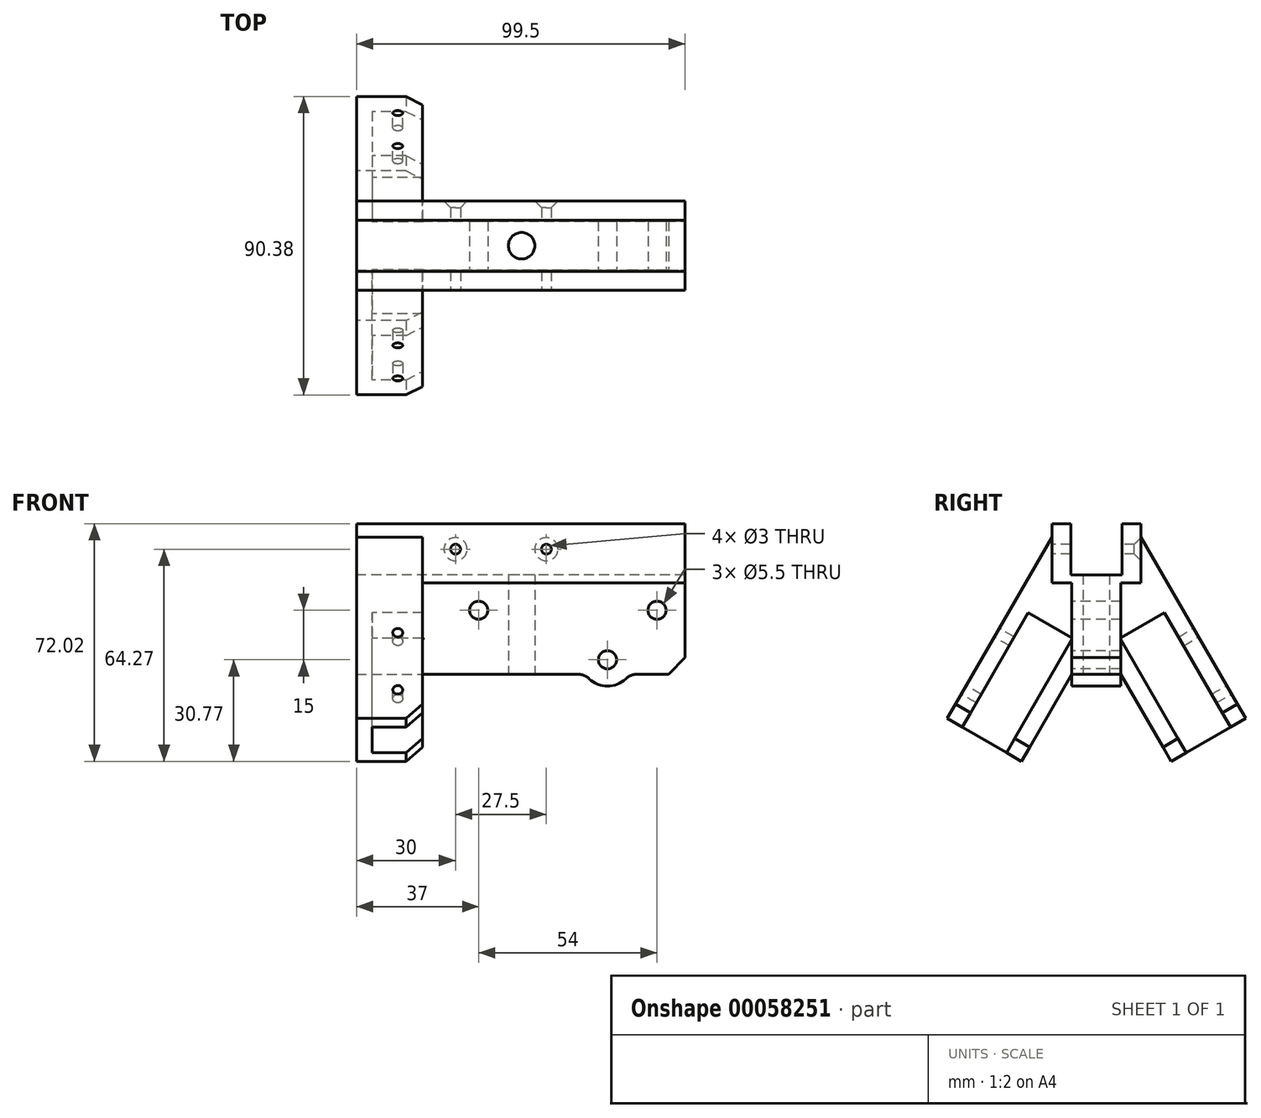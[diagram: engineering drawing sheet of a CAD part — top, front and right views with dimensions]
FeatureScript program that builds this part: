
annotation { "Feature Type Name" : "Feature", "Feature Type Description" : "" }
export const myFeature = defineFeature(function(context is Context, id is Id, definition is map)
    precondition{}
    {
        {
            var Q0;
            Q0=qCreatedBy(makeId("Right.planeOp"),FACE);
            var sketch = newSketch(context, id + "F0", { "sketchPlane" : qUnion([Q0])});
            skLineSegment(sketch, "E0", {"start": v(0, 0) * mm, "end": v(-44.33, -76.78) * mm, "construction": true});
            skLineSegment(sketch, "E1", {"start": v(44.33, -76.78) * mm, "end": v(0, 0) * mm, "construction": true});
            skLineSegment(sketch, "E2.bottom", {"start": v(7.5, -7.5) * mm, "end": v(-7.5, -7.5) * mm});
            skLineSegment(sketch, "E2.top", {"start": v(7.5, 7.5) * mm, "end": v(-7.5, 7.5) * mm});
            skLineSegment(sketch, "E2.left", {"start": v(7.5, -7.5) * mm, "end": v(7.5, 7.5) * mm});
            skLineSegment(sketch, "E2.right", {"start": v(-7.5, -7.5) * mm, "end": v(-7.5, 7.5) * mm});
            skPoint(sketch, "E2.middle", {"position": v(0, 0) * mm});
            skPoint(sketch, "E3", {"position": v(13.5, -23.37) * mm});
            skLineSegment(sketch, "E4", {"start": v(0, 0) * mm, "end": v(0, -80.5) * mm, "construction": true});
            skLineSegment(sketch, "E5", {"start": v(7, -27.12) * mm, "end": v(20, -19.62) * mm, "construction": true});
            skLineSegment(sketch, "E6", {"start": v(8.37, 12.5) * mm, "end": v(45.19, -51.27) * mm});
            skLineSegment(sketch, "E7", {"start": v(45.19, -51.27) * mm, "end": v(33.5, -58.02) * mm, "construction": true});
            skLineSegment(sketch, "E8.MirrorCS", {"start": v(-8.37, 12.5) * mm, "end": v(-45.19, -51.27) * mm});
            skLineSegment(sketch, "E9", {"start": v(-8.37, 12.5) * mm, "end": v(8.37, 12.5) * mm});
            skLineSegment(sketch, "E10", {"start": v(0, -25) * mm, "end": v(22.67, -64.27) * mm});
            skLineSegment(sketch, "E11.MirrorCS", {"start": v(0, -25) * mm, "end": v(-22.67, -64.27) * mm});
            skLineSegment(sketch, "E12", {"start": v(-45.19, -51.27) * mm, "end": v(-22.67, -64.27) * mm});
            skLineSegment(sketch, "E13", {"start": v(22.67, -64.27) * mm, "end": v(45.19, -51.27) * mm});
            skSolve(sketch);
        }
        {
            var Q0;
            Q0 = qSketchRegion(id + "F0", true);
            extrude(context, id + "F1", {"entities" : qUnion([Q0]), "depth" : 20 * mm});
        }
        {
            var Q0;
            Q0=makeQuery(id+"F1.opExtrude","CAP_FACE",FACE,{"disambiguationData":[OSD([sQuery(id+"F0.wireOp",EDGE,"E2.bottom"),sQuery(id+"F0.wireOp",EDGE,"E2.top"),sQuery(id+"F0.wireOp",EDGE,"E2.left"),sQuery(id+"F0.wireOp",EDGE,"E2.right"),sQuery(id+"F0.wireOp",EDGE,"E6"),sQuery(id+"F0.wireOp",EDGE,"E8.MirrorCS"),sQuery(id+"F0.wireOp",EDGE,"E9"),sQuery(id+"F0.wireOp",EDGE,"E10"),sQuery(id+"F0.wireOp",EDGE,"E11.MirrorCS"),sQuery(id+"F0.wireOp",EDGE,"E12"),sQuery(id+"F0.wireOp",EDGE,"E13")])],"isStart":false});
            var sketch = newSketch(context, id + "F2", { "sketchPlane" : qUnion([Q0])});
            skLineSegment(sketch, "E14", {"start": v(0, 0) * mm, "end": v(0, -66.35) * mm, "construction": true});
            skLineSegment(sketch, "E15", {"start": v(-40.42, -54.02) * mm, "end": v(-27.43, -61.52) * mm});
            skLineSegment(sketch, "E16", {"start": v(-27.43, -61.52) * mm, "end": v(-7.43, -26.87) * mm});
            skLineSegment(sketch, "E17", {"start": v(-7.43, -26.87) * mm, "end": v(-20.42, -19.37) * mm});
            skLineSegment(sketch, "E18", {"start": v(-20.42, -19.37) * mm, "end": v(-40.42, -54.02) * mm});
            skPoint(sketch, "E19", {"position": v(-33.93, -57.77) * mm});
            skLineSegment(sketch, "E20.MirrorCS", {"start": v(40.42, -54.02) * mm, "end": v(27.43, -61.52) * mm});
            skLineSegment(sketch, "E21.MirrorCS", {"start": v(27.43, -61.52) * mm, "end": v(7.43, -26.87) * mm});
            skLineSegment(sketch, "E22.MirrorCS", {"start": v(20.42, -19.37) * mm, "end": v(40.42, -54.02) * mm});
            skLineSegment(sketch, "E23.MirrorCS", {"start": v(7.43, -26.87) * mm, "end": v(20.42, -19.37) * mm});
            skSolve(sketch);
        }
        {
            var Q0;
            Q0 = qSketchRegion(id + "F2", true);
            extrude(context, id + "F3", {"entities" : qUnion([Q0]), "operationType" : NewBodyOperationType.REMOVE, "oppositeDirection" : true, "depth" : 15 * mm});
        }
        {
            var Q0;
            Q0=makeQuery(id+"F1.opExtrude","SWEPT_FACE",FACE,{"disambiguationData":[OSD([sQuery(id+"F0.wireOp",EDGE,"E8.MirrorCS")])]});
            var sketch = newSketch(context, id + "F4", { "sketchPlane" : qUnion([Q0])});
            skLineSegment(sketch, "E24.0", {"start": v(5, -67) * mm, "end": v(20, -67) * mm, "construction": true});
            skLineSegment(sketch, "E24.1", {"start": v(5, -27) * mm, "end": v(20, -27) * mm, "construction": true});
            skLineSegment(sketch, "E25", {"start": v(12.5, -27) * mm, "end": v(12.5, -67) * mm, "construction": true});
            skCircle(sketch, "E26", {"center": v(12.5, -37) * mm, "radius": 1.5 * mm});
            skCircle(sketch, "E27", {"center": v(12.5, -57) * mm, "radius": 1.5 * mm});
            skSolve(sketch);
        }
        {
            var Q0;
            Q0 = qSketchRegion(id + "F4", true);
            extrude(context, id + "F5", {"entities" : qUnion([Q0]), "operationType" : NewBodyOperationType.REMOVE, "endBound" : BoundingType.UP_TO_NEXT, "oppositeDirection" : true, "depth" : 25 * mm});
        }
        {
            var Q0;
            Q0=makeQuery(id+"F1.opExtrude","SWEPT_FACE",FACE,{"disambiguationData":[OSD([sQuery(id+"F0.wireOp",EDGE,"E6")])]});
            var sketch = newSketch(context, id + "F6", { "sketchPlane" : qUnion([Q0])});
            skLineSegment(sketch, "E28.0", {"start": v(-5, -67) * mm, "end": v(-20, -67) * mm, "construction": true});
            skLineSegment(sketch, "E28.1", {"start": v(-5, -27) * mm, "end": v(-20, -27) * mm, "construction": true});
            skLineSegment(sketch, "E29", {"start": v(-12.5, -67) * mm, "end": v(-12.5, -27) * mm, "construction": true});
            skCircle(sketch, "E30", {"center": v(-12.5, -57) * mm, "radius": 1.5 * mm});
            skCircle(sketch, "E31", {"center": v(-12.5, -37) * mm, "radius": 1.5 * mm});
            skSolve(sketch);
        }
        {
            var Q0;
            Q0 = qSketchRegion(id + "F6", true);
            extrude(context, id + "F7", {"entities" : qUnion([Q0]), "operationType" : NewBodyOperationType.REMOVE, "endBound" : BoundingType.UP_TO_NEXT, "oppositeDirection" : true, "depth" : 25 * mm});
        }
        {
            var Q0;
            Q0=makeQuery(id+"F1.opExtrude","CAP_FACE",FACE,{"disambiguationData":[OSD([sQuery(id+"F0.wireOp",EDGE,"E2.bottom"),sQuery(id+"F0.wireOp",EDGE,"E2.top"),sQuery(id+"F0.wireOp",EDGE,"E2.left"),sQuery(id+"F0.wireOp",EDGE,"E2.right"),sQuery(id+"F0.wireOp",EDGE,"E6"),sQuery(id+"F0.wireOp",EDGE,"E8.MirrorCS"),sQuery(id+"F0.wireOp",EDGE,"E9"),sQuery(id+"F0.wireOp",EDGE,"E10"),sQuery(id+"F0.wireOp",EDGE,"E11.MirrorCS"),sQuery(id+"F0.wireOp",EDGE,"E12"),sQuery(id+"F0.wireOp",EDGE,"E13")])],"isStart":false});
            var sketch = newSketch(context, id + "F8", { "sketchPlane" : qUnion([Q0])});
            skLineSegment(sketch, "E32.0", {"start": v(-8.37, 12.5) * mm, "end": v(8.37, 12.5) * mm});
            skLineSegment(sketch, "E32.1", {"start": v(-7.5, -7.5) * mm, "end": v(-7.5, 7.5) * mm});
            skLineSegment(sketch, "E32.2", {"start": v(7.5, 7.5) * mm, "end": v(-7.5, 7.5) * mm});
            skLineSegment(sketch, "E32.3", {"start": v(7.5, -7.5) * mm, "end": v(7.5, 7.5) * mm});
            skLineSegment(sketch, "E32.4", {"start": v(7.5, -7.5) * mm, "end": v(-7.5, -7.5) * mm});
            skLineSegment(sketch, "E33", {"start": v(-8.37, 12.5) * mm, "end": v(-13.5, 3.62) * mm});
            skLineSegment(sketch, "E34", {"start": v(-13.5, 3.62) * mm, "end": v(-13.5, -23.37) * mm});
            skLineSegment(sketch, "E35", {"start": v(0, 7.5) * mm, "end": v(0, 0) * mm, "construction": true});
            skLineSegment(sketch, "E36", {"start": v(-13.5, -23.37) * mm, "end": v(-7.43, -26.87) * mm});
            skLineSegment(sketch, "E37.MirrorCS", {"start": v(8.37, 12.5) * mm, "end": v(13.5, 3.62) * mm});
            skLineSegment(sketch, "E38.MirrorCS", {"start": v(13.5, 3.62) * mm, "end": v(13.5, -23.37) * mm});
            skLineSegment(sketch, "E39.MirrorCS", {"start": v(13.5, -23.37) * mm, "end": v(7.43, -26.87) * mm});
            skLineSegment(sketch, "E40", {"start": v(-7.43, -26.87) * mm, "end": v(7.43, -26.87) * mm});
            skSolve(sketch);
        }
        {
            var Q0;
            Q0 = qSketchRegion(id + "F8", true);
            extrude(context, id + "F9", {"entities" : qUnion([Q0]), "operationType" : NewBodyOperationType.ADD, "depth" : 47.5 * mm});
        }
        {
            var Q0;
            Q0=makeQuery(id+"F9.opExtrude","SWEPT_FACE",FACE,{"disambiguationData":[OSD([sQuery(id+"F8.wireOp",EDGE,"E40")])]});
            var sketch = newSketch(context, id + "F10", { "sketchPlane" : qUnion([Q0])});
            skLineSegment(sketch, "E41", {"start": v(50, 7.43) * mm, "end": v(50, -7.43) * mm, "construction": true});
            skCircle(sketch, "E42", {"center": v(50, 0) * mm, "radius": 4 * mm});
            skSolve(sketch);
        }
        {
            var Q0;
            Q0 = qSketchRegion(id + "F10", true);
            extrude(context, id + "F11", {"entities" : qUnion([Q0]), "operationType" : NewBodyOperationType.REMOVE, "endBound" : BoundingType.UP_TO_NEXT, "oppositeDirection" : true, "depth" : 25 * mm});
        }
        {
            var Q0;
            Q0=makeQuery(id+"F9.opExtrude","CAP_FACE",FACE,{"disambiguationData":[OSD([sQuery(id+"F8.wireOp",EDGE,"E32.0"),sQuery(id+"F8.wireOp",EDGE,"E32.1"),sQuery(id+"F8.wireOp",EDGE,"E32.2"),sQuery(id+"F8.wireOp",EDGE,"E32.3"),sQuery(id+"F8.wireOp",EDGE,"E32.4"),sQuery(id+"F8.wireOp",EDGE,"E33"),sQuery(id+"F8.wireOp",EDGE,"E34"),sQuery(id+"F8.wireOp",EDGE,"E36"),sQuery(id+"F8.wireOp",EDGE,"E37.MirrorCS"),sQuery(id+"F8.wireOp",EDGE,"E38.MirrorCS"),sQuery(id+"F8.wireOp",EDGE,"E39.MirrorCS"),sQuery(id+"F8.wireOp",EDGE,"E40")])],"isStart":false});
            var sketch = newSketch(context, id + "F12", { "sketchPlane" : qUnion([Q0])});
            skLineSegment(sketch, "E43.0", {"start": v(-4, -7.5) * mm, "end": v(4, -7.5) * mm, "construction": true});
            skLineSegment(sketch, "E44", {"start": v(-4, -7.5) * mm, "end": v(-12.87, -7.5) * mm, "construction": true});
            skPoint(sketch, "E45", {"position": v(-7.87, -7.5) * mm});
            skLineSegment(sketch, "E46", {"start": v(-7.87, -7.5) * mm, "end": v(-7.87, -25.06) * mm, "construction": true});
            skLineSegment(sketch, "E47", {"start": v(-24.1, -18.5) * mm, "end": v(2.06, -18.5) * mm, "construction": true});
            skLineSegment(sketch, "E48.0", {"start": v(-7.43, -26.87) * mm, "end": v(-13.5, -23.37) * mm});
            skLineSegment(sketch, "E49", {"start": v(-13.5, -23.37) * mm, "end": v(-13.5, -10.25) * mm});
            skLineSegment(sketch, "E50", {"start": v(-13.5, -10.25) * mm, "end": v(-7.43, -10.25) * mm});
            skLineSegment(sketch, "E51", {"start": v(-7.43, -10.25) * mm, "end": v(-7.43, -26.87) * mm});
            skLineSegment(sketch, "E52", {"start": v(0, 0) * mm, "end": v(0, 7.5) * mm, "construction": true});
            skLineSegment(sketch, "E53.MirrorCS", {"start": v(7.43, -26.87) * mm, "end": v(13.5, -23.37) * mm});
            skLineSegment(sketch, "E54.MirrorCS", {"start": v(7.43, -10.25) * mm, "end": v(7.43, -26.87) * mm});
            skLineSegment(sketch, "E55.MirrorCS", {"start": v(13.5, -10.25) * mm, "end": v(7.43, -10.25) * mm});
            skLineSegment(sketch, "E56.MirrorCS", {"start": v(13.5, -23.37) * mm, "end": v(13.5, -10.25) * mm});
            skSolve(sketch);
        }
        {
            var Q0;
            Q0 = qSketchRegion(id + "F12", true);
            var Q1;
            {var subQ0=sQuery(id+"F0.wireOp",EDGE,"E8.MirrorCS");var subQ1=sQuery(id+"F0.wireOp",EDGE,"E12");Q1=makeQuery(id+"F9.boolean.opBoolean","SPLIT",FACE,{"disambiguationData":[TD([makeQuery(id+"F1.opExtrude","SWEPT_FACE",FACE,{"disambiguationData":[OSD([subQ0])]})])],"derivedFrom":makeQuery(id+"F1.opExtrude","CAP_FACE",FACE,{"disambiguationData":[OSD([sQuery(id+"F0.wireOp",EDGE,"E2.bottom"),sQuery(id+"F0.wireOp",EDGE,"E2.top"),sQuery(id+"F0.wireOp",EDGE,"E2.left"),sQuery(id+"F0.wireOp",EDGE,"E2.right"),sQuery(id+"F0.wireOp",EDGE,"E6"),subQ0,sQuery(id+"F0.wireOp",EDGE,"E9"),sQuery(id+"F0.wireOp",EDGE,"E10"),sQuery(id+"F0.wireOp",EDGE,"E11.MirrorCS"),subQ1,sQuery(id+"F0.wireOp",EDGE,"E13")])],"isStart":false})});}
            extrude(context, id + "F13", {"entities" : qUnion([Q0]), "operationType" : NewBodyOperationType.REMOVE, "endBound" : BoundingType.UP_TO_SURFACE, "oppositeDirection" : true, "endBoundEntityFace" : qUnion([Q1]), "depth" : 25 * mm});
        }
        {
            var Q0;
            Q0=makeQuery(id+"F13.boolean.opBoolean","COPY",FACE,{"derivedFrom":makeQuery(id+"F13.opExtrude","SWEPT_FACE",FACE,{"disambiguationData":[OSD([sQuery(id+"F12.wireOp",EDGE,"E51")])]})});
            var sketch = newSketch(context, id + "F14", { "sketchPlane" : qUnion([Q0])});
            skLineSegment(sketch, "E57.0", {"start": v(54, -26.87) * mm, "end": v(46, -26.87) * mm, "construction": true});
            skCircle(sketch, "E58", {"center": v(37, -18.5) * mm, "radius": 2.75 * mm});
            skLineSegment(sketch, "E59", {"start": v(50, -26.87) * mm, "end": v(50, -10.25) * mm, "construction": true});
            skLineSegment(sketch, "E60", {"start": v(33, -26.87) * mm, "end": v(33, -10.25) * mm, "construction": true});
            skCircle(sketch, "E61", {"center": v(37, -18.5) * mm, "radius": 8 * mm, "construction": true});
            skCircle(sketch, "E62", {"center": v(37, -18.5) * mm, "radius": 7.5 * mm, "construction": true});
            skPoint(sketch, "E63", {"position": v(29.5, -18.5) * mm});
            skSolve(sketch);
        }
        {
            var Q0;
            Q0 = qSketchRegion(id + "F14", true);
            extrude(context, id + "F15", {"entities" : qUnion([Q0]), "operationType" : NewBodyOperationType.REMOVE, "endBound" : BoundingType.THROUGH_ALL, "oppositeDirection" : true, "depth" : 25 * mm});
        }
        {
            var Q0;
            Q0=makeQuery(id+"F9.opExtrude","CAP_FACE",FACE,{"disambiguationData":[OSD([sQuery(id+"F8.wireOp",EDGE,"E32.0"),sQuery(id+"F8.wireOp",EDGE,"E32.1"),sQuery(id+"F8.wireOp",EDGE,"E32.2"),sQuery(id+"F8.wireOp",EDGE,"E32.3"),sQuery(id+"F8.wireOp",EDGE,"E32.4"),sQuery(id+"F8.wireOp",EDGE,"E33"),sQuery(id+"F8.wireOp",EDGE,"E34"),sQuery(id+"F8.wireOp",EDGE,"E36"),sQuery(id+"F8.wireOp",EDGE,"E37.MirrorCS"),sQuery(id+"F8.wireOp",EDGE,"E38.MirrorCS"),sQuery(id+"F8.wireOp",EDGE,"E39.MirrorCS"),sQuery(id+"F8.wireOp",EDGE,"E40")])],"isStart":true});
            var Q1;
            Q1=makeQuery(id+"F1.opExtrude","CAP_FACE",FACE,{"disambiguationData":[OSD([sQuery(id+"F0.wireOp",EDGE,"E2.bottom"),sQuery(id+"F0.wireOp",EDGE,"E2.top"),sQuery(id+"F0.wireOp",EDGE,"E2.left"),sQuery(id+"F0.wireOp",EDGE,"E2.right"),sQuery(id+"F0.wireOp",EDGE,"E6"),sQuery(id+"F0.wireOp",EDGE,"E8.MirrorCS"),sQuery(id+"F0.wireOp",EDGE,"E9"),sQuery(id+"F0.wireOp",EDGE,"E10"),sQuery(id+"F0.wireOp",EDGE,"E11.MirrorCS"),sQuery(id+"F0.wireOp",EDGE,"E12"),sQuery(id+"F0.wireOp",EDGE,"E13")])],"isStart":true});
            extrude(context, id + "F16", {"entities" : qUnion([Q0]), "operationType" : NewBodyOperationType.ADD, "endBound" : BoundingType.UP_TO_SURFACE, "endBoundEntityFace" : qUnion([Q1]), "depth" : 25 * mm});
        }
        {
            var Q0;
            {var subQ0=sQuery(id+"F8.wireOp",EDGE,"E40");Q0=makeQuery(id+"F16.boolean.opBoolean","MERGE",FACE,{"derivedFrom":[makeQuery(id+"F9.opExtrude","SWEPT_FACE",FACE,{"disambiguationData":[OSD([subQ0])]}),makeQuery(id+"F16.opExtrude","SWEPT_FACE",FACE,{"disambiguationData":[OSD([subQ0])]})]});}
            var sketch = newSketch(context, id + "F17", { "sketchPlane" : qUnion([Q0])});
            skLineSegment(sketch, "E64.bottom", {"start": v(67.5, 7.43) * mm, "end": v(0, 7.43) * mm});
            skLineSegment(sketch, "E64.top", {"start": v(67.5, -7.43) * mm, "end": v(0, -7.43) * mm});
            skLineSegment(sketch, "E64.left", {"start": v(67.5, 7.43) * mm, "end": v(67.5, -7.43) * mm});
            skLineSegment(sketch, "E64.right", {"start": v(0, 7.43) * mm, "end": v(0, -7.43) * mm});
            skCircle(sketch, "E65.0", {"center": v(50, 0) * mm, "radius": 4 * mm});
            skSolve(sketch);
        }
        {
            var Q0;
            Q0 = qSketchRegion(id + "F17", true);
            var Q1;
            Q1=makeQuery(id+"F1.opExtrude","SWEPT_FACE",FACE,{"disambiguationData":[OSD([sQuery(id+"F0.wireOp",EDGE,"E11.MirrorCS")])]});
            var Q2;
            Q2=makeQuery(id+"F1.opExtrude","CAP_VERTEX",VERTEX,{"disambiguationData":[OSD([sQuery(id+"F0.wireOp",EDGE,"E11.MirrorCS"),sQuery(id+"F0.wireOp",EDGE,"E12")])],"isStart":false});
            extrude(context, id + "F18", {"entities" : qUnion([Q0]), "operationType" : NewBodyOperationType.ADD, "endBound" : BoundingType.UP_TO_VERTEX, "endBoundEntityFace" : qUnion([Q1]), "endBoundEntityVertex" : qUnion([Q2]), "depth" : 25 * mm});
        }
        {
            var Q0;
            {var subQ0=sQuery(id+"F0.wireOp",EDGE,"E13");var subQ1=sQuery(id+"F0.wireOp",EDGE,"E12");var subQ2=sQuery(id+"F0.wireOp",EDGE,"E11.MirrorCS");var subQ3=sQuery(id+"F0.wireOp",EDGE,"E10");var subQ4=sQuery(id+"F0.wireOp",EDGE,"E9");var subQ5=sQuery(id+"F0.wireOp",EDGE,"E8.MirrorCS");var subQ6=sQuery(id+"F0.wireOp",EDGE,"E6");var subQ7=sQuery(id+"F0.wireOp",EDGE,"E2.right");var subQ8=sQuery(id+"F0.wireOp",EDGE,"E2.left");var subQ9=sQuery(id+"F0.wireOp",EDGE,"E2.top");var subQ10=sQuery(id+"F0.wireOp",EDGE,"E2.bottom");Q0=makeQuery(id+"F18.boolean.opBoolean","MERGE",FACE,{"derivedFrom":[makeQuery(id+"F16.boolean.opBoolean","MERGE",FACE,{"derivedFrom":[makeQuery(id+"F1.opExtrude","CAP_FACE",FACE,{"disambiguationData":[OSD([subQ10,subQ9,subQ8,subQ7,subQ6,subQ5,subQ4,subQ3,subQ2,subQ1,subQ0])],"isStart":true}),makeQuery(id+"F16.opExtrude","CAP_FACE",FACE,{"disambiguationData":[OSD([subQ10,subQ9,subQ8,subQ7,subQ6,subQ5,subQ4,subQ3,subQ2,subQ1,subQ0])],"isStart":false})]}),makeQuery(id+"F18.opExtrude","SWEPT_FACE",FACE,{"disambiguationData":[OSD([sQuery(id+"F17.wireOp",EDGE,"E64.right")])]})]});}
            var sketch = newSketch(context, id + "F19", { "sketchPlane" : qUnion([Q0])});
            skLineSegment(sketch, "E66.bottom", {"start": v(7.43, -64.27) * mm, "end": v(-7.43, -64.27) * mm});
            skLineSegment(sketch, "E66.top", {"start": v(7.43, -37.87) * mm, "end": v(-7.43, -37.87) * mm});
            skLineSegment(sketch, "E66.left", {"start": v(7.43, -64.27) * mm, "end": v(7.43, -37.87) * mm});
            skLineSegment(sketch, "E66.right", {"start": v(-7.43, -64.27) * mm, "end": v(-7.43, -37.87) * mm});
            skSolve(sketch);
        }
        {
            var Q0;
            Q0 = qSketchRegion(id + "F19", true);
            extrude(context, id + "F20", {"entities" : qUnion([Q0]), "operationType" : NewBodyOperationType.REMOVE, "endBound" : BoundingType.THROUGH_ALL, "oppositeDirection" : true, "depth" : 25 * mm});
        }
        {
            var Q0;
            {var subQ0=sQuery(id+"F0.wireOp",EDGE,"E12");var subQ1=sQuery(id+"F0.wireOp",EDGE,"E8.MirrorCS");Q0=makeQuery(id+"F3.boolean.opBoolean","SPLIT",EDGE,{"disambiguationData":[TD([makeQuery(id+"F1.opExtrude","SWEPT_FACE",FACE,{"disambiguationData":[OSD([subQ1])]})])],"derivedFrom":makeQuery(id+"F1.opExtrude","CAP_EDGE",EDGE,{"disambiguationData":[OSD([subQ0])],"isStart":false})});}
            var Q1;
            {var subQ0=sQuery(id+"F0.wireOp",EDGE,"E12");var subQ1=sQuery(id+"F0.wireOp",EDGE,"E11.MirrorCS");Q1=makeQuery(id+"F3.boolean.opBoolean","SPLIT",EDGE,{"disambiguationData":[TD([makeQuery(id+"F1.opExtrude","SWEPT_FACE",FACE,{"disambiguationData":[OSD([subQ1])]})])],"derivedFrom":makeQuery(id+"F1.opExtrude","CAP_EDGE",EDGE,{"disambiguationData":[OSD([subQ0])],"isStart":false})});}
            var Q2;
            {var subQ0=sQuery(id+"F0.wireOp",EDGE,"E13");var subQ1=sQuery(id+"F0.wireOp",EDGE,"E10");Q2=makeQuery(id+"F3.boolean.opBoolean","SPLIT",EDGE,{"disambiguationData":[TD([makeQuery(id+"F1.opExtrude","SWEPT_FACE",FACE,{"disambiguationData":[OSD([subQ1])]})])],"derivedFrom":makeQuery(id+"F1.opExtrude","CAP_EDGE",EDGE,{"disambiguationData":[OSD([subQ0])],"isStart":false})});}
            var Q3;
            {var subQ0=sQuery(id+"F0.wireOp",EDGE,"E13");var subQ1=sQuery(id+"F0.wireOp",EDGE,"E6");Q3=makeQuery(id+"F3.boolean.opBoolean","SPLIT",EDGE,{"disambiguationData":[TD([makeQuery(id+"F1.opExtrude","SWEPT_FACE",FACE,{"disambiguationData":[OSD([subQ1])]})])],"derivedFrom":makeQuery(id+"F1.opExtrude","CAP_EDGE",EDGE,{"disambiguationData":[OSD([subQ0])],"isStart":false})});}
            chamfer(context, id + "F21", {"entities" : qUnion([Q0, Q1, Q2, Q3]), "width" : 5 * mm, "tangentPropagation" : true});
        }
        {
            var Q0;
            Q0=makeQuery(id+"F9.opExtrude","SWEPT_FACE",FACE,{"disambiguationData":[OSD([sQuery(id+"F8.wireOp",EDGE,"E34")])]});
            var sketch = newSketch(context, id + "F22", { "sketchPlane" : qUnion([Q0])});
            skLineSegment(sketch, "E67.0", {"start": v(67.5, -7.5) * mm, "end": v(67.5, 7.5) * mm, "construction": true});
            skLineSegment(sketch, "E68", {"start": v(67.5, 0) * mm, "end": v(20, 0) * mm, "construction": true});
            skCircle(sketch, "E69", {"center": v(30, 0) * mm, "radius": 1.5 * mm});
            skCircle(sketch, "E70", {"center": v(57.5, 0) * mm, "radius": 1.5 * mm});
            skSolve(sketch);
        }
        {
            var Q0;
            Q0 = qSketchRegion(id + "F22", true);
            extrude(context, id + "F23", {"entities" : qUnion([Q0]), "operationType" : NewBodyOperationType.REMOVE, "endBound" : BoundingType.THROUGH_ALL, "oppositeDirection" : true, "depth" : 25 * mm});
        }
        {
            var Q0;
            {var subQ0=sQuery(id+"F0.wireOp",EDGE,"E13");var subQ1=sQuery(id+"F0.wireOp",EDGE,"E12");var subQ2=sQuery(id+"F0.wireOp",EDGE,"E11.MirrorCS");var subQ3=sQuery(id+"F0.wireOp",EDGE,"E10");var subQ4=sQuery(id+"F0.wireOp",EDGE,"E9");var subQ5=sQuery(id+"F0.wireOp",EDGE,"E8.MirrorCS");var subQ6=sQuery(id+"F0.wireOp",EDGE,"E6");var subQ7=sQuery(id+"F0.wireOp",EDGE,"E2.right");var subQ8=sQuery(id+"F0.wireOp",EDGE,"E2.left");var subQ9=sQuery(id+"F0.wireOp",EDGE,"E2.top");var subQ10=sQuery(id+"F0.wireOp",EDGE,"E2.bottom");Q0=makeQuery(id+"F18.boolean.opBoolean","MERGE",FACE,{"derivedFrom":[makeQuery(id+"F16.boolean.opBoolean","MERGE",FACE,{"derivedFrom":[makeQuery(id+"F1.opExtrude","CAP_FACE",FACE,{"disambiguationData":[OSD([subQ10,subQ9,subQ8,subQ7,subQ6,subQ5,subQ4,subQ3,subQ2,subQ1,subQ0])],"isStart":true}),makeQuery(id+"F16.opExtrude","CAP_FACE",FACE,{"disambiguationData":[OSD([subQ10,subQ9,subQ8,subQ7,subQ6,subQ5,subQ4,subQ3,subQ2,subQ1,subQ0])],"isStart":false})]}),makeQuery(id+"F18.opExtrude","SWEPT_FACE",FACE,{"disambiguationData":[OSD([sQuery(id+"F17.wireOp",EDGE,"E64.right")])]})]});}
            var sketch = newSketch(context, id + "F24", { "sketchPlane" : qUnion([Q0])});
            skLineSegment(sketch, "E71.bottom", {"start": v(7.75, -7.75) * mm, "end": v(-7.75, -7.75) * mm});
            skLineSegment(sketch, "E71.top", {"start": v(7.75, 7.75) * mm, "end": v(-7.75, 7.75) * mm});
            skLineSegment(sketch, "E71.left", {"start": v(7.75, -7.75) * mm, "end": v(7.75, 7.75) * mm});
            skLineSegment(sketch, "E71.right", {"start": v(-7.75, -7.75) * mm, "end": v(-7.75, 7.75) * mm});
            skPoint(sketch, "E71.middle", {"position": v(0, 0) * mm});
            skSolve(sketch);
        }
        {
            var Q0;
            Q0 = qSketchRegion(id + "F24", true);
            extrude(context, id + "F25", {"entities" : qUnion([Q0]), "operationType" : NewBodyOperationType.REMOVE, "endBound" : BoundingType.THROUGH_ALL, "oppositeDirection" : true, "depth" : 25 * mm});
        }
        {
            var Q0;
            Q0=makeQuery(id+"F9.boolean.opBoolean","MERGE",FACE,{"derivedFrom":[makeQuery(id+"F3.boolean.opBoolean","COPY",FACE,{"derivedFrom":makeQuery(id+"F3.opExtrude","SWEPT_FACE",FACE,{"disambiguationData":[OSD([sQuery(id+"F2.wireOp",EDGE,"E17")])]})}),makeQuery(id+"F9.opExtrude","SWEPT_FACE",FACE,{"disambiguationData":[OSD([sQuery(id+"F8.wireOp",EDGE,"E36")])]})]});
            var sketch = newSketch(context, id + "F26", { "sketchPlane" : qUnion([Q0])});
            skLineSegment(sketch, "E72", {"start": v(20, 8) * mm, "end": v(5, -7) * mm, "construction": true});
            skLineSegment(sketch, "E73.bottom", {"start": v(20.25, -7.25) * mm, "end": v(4.75, -7.25) * mm});
            skLineSegment(sketch, "E73.top", {"start": v(20.25, 8.25) * mm, "end": v(4.75, 8.25) * mm});
            skLineSegment(sketch, "E73.left", {"start": v(20.25, -7.25) * mm, "end": v(20.25, 8.25) * mm});
            skLineSegment(sketch, "E73.right", {"start": v(4.75, -7.25) * mm, "end": v(4.75, 8.25) * mm});
            skPoint(sketch, "E73.middle", {"position": v(12.5, 0.5) * mm});
            skSolve(sketch);
        }
        {
            var Q0;
            Q0 = qSketchRegion(id + "F26", true);
            extrude(context, id + "F27", {"entities" : qUnion([Q0]), "operationType" : NewBodyOperationType.REMOVE, "endBound" : BoundingType.THROUGH_ALL, "depth" : 25 * mm});
        }
        {
            var Q0;
            Q0=makeQuery(id+"F9.boolean.opBoolean","MERGE",FACE,{"derivedFrom":[makeQuery(id+"F3.boolean.opBoolean","COPY",FACE,{"derivedFrom":makeQuery(id+"F3.opExtrude","SWEPT_FACE",FACE,{"disambiguationData":[OSD([sQuery(id+"F2.wireOp",EDGE,"E23.MirrorCS")])]})}),makeQuery(id+"F9.opExtrude","SWEPT_FACE",FACE,{"disambiguationData":[OSD([sQuery(id+"F8.wireOp",EDGE,"E39.MirrorCS")])]})]});
            var sketch = newSketch(context, id + "F28", { "sketchPlane" : qUnion([Q0])});
            skLineSegment(sketch, "E74", {"start": v(5, 7) * mm, "end": v(20, -8) * mm, "construction": true});
            skLineSegment(sketch, "E75.bottom", {"start": v(20.25, -8.25) * mm, "end": v(4.75, -8.25) * mm});
            skLineSegment(sketch, "E75.top", {"start": v(20.25, 7.25) * mm, "end": v(4.75, 7.25) * mm});
            skLineSegment(sketch, "E75.left", {"start": v(20.25, -8.25) * mm, "end": v(20.25, 7.25) * mm});
            skLineSegment(sketch, "E75.right", {"start": v(4.75, -8.25) * mm, "end": v(4.75, 7.25) * mm});
            skPoint(sketch, "E75.middle", {"position": v(12.5, -0.5) * mm});
            skSolve(sketch);
        }
        {
            var Q0;
            Q0 = qSketchRegion(id + "F28", true);
            extrude(context, id + "F29", {"entities" : qUnion([Q0]), "operationType" : NewBodyOperationType.REMOVE, "endBound" : BoundingType.THROUGH_ALL, "depth" : 25 * mm});
        }
        {
            var Q0;
            Q0=makeQuery(id+"F18.boolean.opBoolean","MERGE",FACE,{"derivedFrom":[makeQuery(id+"F9.opExtrude","CAP_FACE",FACE,{"disambiguationData":[OSD([sQuery(id+"F8.wireOp",EDGE,"E32.0"),sQuery(id+"F8.wireOp",EDGE,"E32.1"),sQuery(id+"F8.wireOp",EDGE,"E32.2"),sQuery(id+"F8.wireOp",EDGE,"E32.3"),sQuery(id+"F8.wireOp",EDGE,"E32.4"),sQuery(id+"F8.wireOp",EDGE,"E33"),sQuery(id+"F8.wireOp",EDGE,"E34"),sQuery(id+"F8.wireOp",EDGE,"E36"),sQuery(id+"F8.wireOp",EDGE,"E37.MirrorCS"),sQuery(id+"F8.wireOp",EDGE,"E38.MirrorCS"),sQuery(id+"F8.wireOp",EDGE,"E39.MirrorCS"),sQuery(id+"F8.wireOp",EDGE,"E40")])],"isStart":false}),makeQuery(id+"F18.opExtrude","SWEPT_FACE",FACE,{"disambiguationData":[OSD([sQuery(id+"F17.wireOp",EDGE,"E64.left")])]})]});
            extrude(context, id + "F30", {"entities" : qUnion([Q0]), "operationType" : NewBodyOperationType.ADD, "depth" : 32 * mm});
        }
        {
            var Q0;
            {var subQ0=sQuery(id+"F17.wireOp",EDGE,"E64.bottom");var subQ1=sQuery(id+"F12.wireOp",EDGE,"E51");Q0=makeQuery(id+"F30.boolean.opBoolean","MERGE",FACE,{"derivedFrom":[makeQuery(id+"F18.boolean.opBoolean","MERGE",FACE,{"derivedFrom":[makeQuery(id+"F13.boolean.opBoolean","COPY",FACE,{"derivedFrom":makeQuery(id+"F13.opExtrude","SWEPT_FACE",FACE,{"disambiguationData":[OSD([subQ1])]})}),makeQuery(id+"F18.opExtrude","SWEPT_FACE",FACE,{"disambiguationData":[OSD([subQ0])]})]}),makeQuery(id+"F30.opExtrude","SWEPT_FACE",FACE,{"disambiguationData":[OSD([subQ1,subQ0,sQuery(id+"F17.wireOp",EDGE,"E64.left")])]})]});}
            var sketch = newSketch(context, id + "F31", { "sketchPlane" : qUnion([Q0])});
            skLineSegment(sketch, "E76", {"start": v(37, -18.5) * mm, "end": v(91, -18.5) * mm, "construction": true});
            skCircle(sketch, "E77", {"center": v(91, -18.5) * mm, "radius": 2.75 * mm});
            skCircle(sketch, "E78", {"center": v(76, -33.5) * mm, "radius": 2.75 * mm});
            skCircle(sketch, "E79", {"center": v(91, -18.5) * mm, "radius": 8 * mm, "construction": true});
            skCircle(sketch, "E80", {"center": v(76, -33.5) * mm, "radius": 8 * mm, "construction": true});
            skPoint(sketch, "E81", {"position": v(83, -18.5) * mm});
            skPoint(sketch, "E82", {"position": v(84, -33.5) * mm});
            skCircle(sketch, "E83", {"center": v(76, -33.5) * mm, "radius": 7.5 * mm, "construction": true});
            skCircle(sketch, "E84", {"center": v(91, -18.5) * mm, "radius": 7.5 * mm, "construction": true});
            skLineSegment(sketch, "E85", {"start": v(76, -33.5) * mm, "end": v(76, -26) * mm, "construction": true});
            skLineSegment(sketch, "E86", {"start": v(76, -26) * mm, "end": v(91, -26) * mm, "construction": true});
            skLineSegment(sketch, "E87", {"start": v(91, -26) * mm, "end": v(91, -18.5) * mm, "construction": true});
            skLineSegment(sketch, "E88", {"start": v(76, -33.5) * mm, "end": v(83.5, -33.5) * mm, "construction": true});
            skLineSegment(sketch, "E89", {"start": v(83.5, -33.5) * mm, "end": v(83.5, -18.5) * mm, "construction": true});
            skLineSegment(sketch, "E90.0", {"start": v(54, -37.87) * mm, "end": v(46, -37.87) * mm, "construction": true});
            skLineSegment(sketch, "E91", {"start": v(50, -37.87) * mm, "end": v(50, -18.5) * mm, "construction": true});
            skLineSegment(sketch, "E92", {"start": v(68, -18.5) * mm, "end": v(68, -37.87) * mm, "construction": true});
            skSolve(sketch);
        }
        {
            var Q0;
            Q0 = qSketchRegion(id + "F31", true);
            extrude(context, id + "F32", {"entities" : qUnion([Q0]), "operationType" : NewBodyOperationType.REMOVE, "endBound" : BoundingType.THROUGH_ALL, "oppositeDirection" : true, "depth" : 25 * mm});
        }
        {
            var Q0;
            {var subQ0=sQuery(id+"F17.wireOp",EDGE,"E64.bottom");var subQ1=sQuery(id+"F12.wireOp",EDGE,"E51");Q0=makeQuery(id+"F30.boolean.opBoolean","MERGE",FACE,{"derivedFrom":[makeQuery(id+"F18.boolean.opBoolean","MERGE",FACE,{"derivedFrom":[makeQuery(id+"F13.boolean.opBoolean","COPY",FACE,{"derivedFrom":makeQuery(id+"F13.opExtrude","SWEPT_FACE",FACE,{"disambiguationData":[OSD([subQ1])]})}),makeQuery(id+"F18.opExtrude","SWEPT_FACE",FACE,{"disambiguationData":[OSD([subQ0])]})]}),makeQuery(id+"F30.opExtrude","SWEPT_FACE",FACE,{"disambiguationData":[OSD([subQ1,subQ0,sQuery(id+"F17.wireOp",EDGE,"E64.left")])]})]});}
            var sketch = newSketch(context, id + "F33", { "sketchPlane" : qUnion([Q0])});
            skCircle(sketch, "E93", {"center": v(76, -33.5) * mm, "radius": 8 * mm});
            skCircle(sketch, "E94.0", {"center": v(76, -33.5) * mm, "radius": 2.75 * mm});
            skSolve(sketch);
        }
        {
            var Q0;
            Q0 = qSketchRegion(id + "F33", true);
            var Q1;
            {var subQ0=sQuery(id+"F17.wireOp",EDGE,"E64.top");var subQ1=sQuery(id+"F12.wireOp",EDGE,"E54.MirrorCS");Q1=makeQuery(id+"F30.boolean.opBoolean","MERGE",FACE,{"derivedFrom":[makeQuery(id+"F18.boolean.opBoolean","MERGE",FACE,{"derivedFrom":[makeQuery(id+"F13.boolean.opBoolean","COPY",FACE,{"derivedFrom":makeQuery(id+"F13.opExtrude","SWEPT_FACE",FACE,{"disambiguationData":[OSD([subQ1])]})}),makeQuery(id+"F18.opExtrude","SWEPT_FACE",FACE,{"disambiguationData":[OSD([subQ0])]})]}),makeQuery(id+"F30.opExtrude","SWEPT_FACE",FACE,{"disambiguationData":[OSD([subQ1,subQ0,sQuery(id+"F17.wireOp",EDGE,"E64.left")])]})]});}
            extrude(context, id + "F34", {"entities" : qUnion([Q0]), "operationType" : NewBodyOperationType.ADD, "endBound" : BoundingType.UP_TO_SURFACE, "oppositeDirection" : true, "endBoundEntityFace" : qUnion([Q1]), "depth" : 25 * mm});
        }
        {
            var Q0;
            Q0=makeQuery(id+"F30.opExtrude","CAP_FACE",FACE,{"disambiguationData":[OSD([sQuery(id+"F8.wireOp",EDGE,"E32.0"),sQuery(id+"F8.wireOp",EDGE,"E32.1"),sQuery(id+"F8.wireOp",EDGE,"E32.2"),sQuery(id+"F8.wireOp",EDGE,"E32.3"),sQuery(id+"F8.wireOp",EDGE,"E32.4"),sQuery(id+"F8.wireOp",EDGE,"E33"),sQuery(id+"F8.wireOp",EDGE,"E34"),sQuery(id+"F8.wireOp",EDGE,"E36"),sQuery(id+"F8.wireOp",EDGE,"E37.MirrorCS"),sQuery(id+"F8.wireOp",EDGE,"E38.MirrorCS"),sQuery(id+"F8.wireOp",EDGE,"E39.MirrorCS"),sQuery(id+"F8.wireOp",EDGE,"E40"),sQuery(id+"F17.wireOp",EDGE,"E64.left")])],"isStart":false});
            var sketch = newSketch(context, id + "F35", { "sketchPlane" : qUnion([Q0])});
            skLineSegment(sketch, "E95.0", {"start": v(-8.37, 12.5) * mm, "end": v(-13.5, 3.62) * mm});
            skLineSegment(sketch, "E96", {"start": v(-8.37, 12.5) * mm, "end": v(-13.5, 12.5) * mm});
            skLineSegment(sketch, "E97", {"start": v(-13.5, 12.5) * mm, "end": v(-13.5, 3.62) * mm});
            skLineSegment(sketch, "E98", {"start": v(0, 0) * mm, "end": v(0, -19.5) * mm, "construction": true});
            skLineSegment(sketch, "E99.MirrorCS", {"start": v(8.37, 12.5) * mm, "end": v(13.5, 12.5) * mm});
            skLineSegment(sketch, "E100.MirrorCS", {"start": v(13.5, 12.5) * mm, "end": v(13.5, 3.62) * mm});
            skLineSegment(sketch, "E101.MirrorCS", {"start": v(8.37, 12.5) * mm, "end": v(13.5, 3.62) * mm});
            skSolve(sketch);
        }
        {
            var Q0;
            Q0 = qSketchRegion(id + "F35", true);
            var Q1;
            {var subQ0=sQuery(id+"F0.wireOp",EDGE,"E13");var subQ1=sQuery(id+"F0.wireOp",EDGE,"E12");var subQ2=sQuery(id+"F0.wireOp",EDGE,"E11.MirrorCS");var subQ3=sQuery(id+"F0.wireOp",EDGE,"E10");var subQ4=sQuery(id+"F0.wireOp",EDGE,"E9");var subQ5=sQuery(id+"F0.wireOp",EDGE,"E8.MirrorCS");var subQ6=sQuery(id+"F0.wireOp",EDGE,"E6");var subQ7=sQuery(id+"F0.wireOp",EDGE,"E2.right");var subQ8=sQuery(id+"F0.wireOp",EDGE,"E2.left");var subQ9=sQuery(id+"F0.wireOp",EDGE,"E2.top");var subQ10=sQuery(id+"F0.wireOp",EDGE,"E2.bottom");Q1=makeQuery(id+"F18.boolean.opBoolean","MERGE",FACE,{"derivedFrom":[makeQuery(id+"F16.boolean.opBoolean","MERGE",FACE,{"derivedFrom":[makeQuery(id+"F1.opExtrude","CAP_FACE",FACE,{"disambiguationData":[OSD([subQ10,subQ9,subQ8,subQ7,subQ6,subQ5,subQ4,subQ3,subQ2,subQ1,subQ0])],"isStart":true}),makeQuery(id+"F16.opExtrude","CAP_FACE",FACE,{"disambiguationData":[OSD([subQ10,subQ9,subQ8,subQ7,subQ6,subQ5,subQ4,subQ3,subQ2,subQ1,subQ0])],"isStart":false})]}),makeQuery(id+"F18.opExtrude","SWEPT_FACE",FACE,{"disambiguationData":[OSD([sQuery(id+"F17.wireOp",EDGE,"E64.right")])]})]});}
            extrude(context, id + "F36", {"entities" : qUnion([Q0]), "operationType" : NewBodyOperationType.ADD, "endBound" : BoundingType.UP_TO_SURFACE, "oppositeDirection" : true, "endBoundEntityFace" : qUnion([Q1]), "depth" : 25 * mm});
        }
        {
            var Q0;
            Q0=makeQuery(id+"F36.boolean.opBoolean","MERGE",FACE,{"derivedFrom":[makeQuery(id+"F30.opExtrude","CAP_FACE",FACE,{"disambiguationData":[OSD([sQuery(id+"F8.wireOp",EDGE,"E32.0"),sQuery(id+"F8.wireOp",EDGE,"E32.1"),sQuery(id+"F8.wireOp",EDGE,"E32.2"),sQuery(id+"F8.wireOp",EDGE,"E32.3"),sQuery(id+"F8.wireOp",EDGE,"E32.4"),sQuery(id+"F8.wireOp",EDGE,"E33"),sQuery(id+"F8.wireOp",EDGE,"E34"),sQuery(id+"F8.wireOp",EDGE,"E36"),sQuery(id+"F8.wireOp",EDGE,"E37.MirrorCS"),sQuery(id+"F8.wireOp",EDGE,"E38.MirrorCS"),sQuery(id+"F8.wireOp",EDGE,"E39.MirrorCS"),sQuery(id+"F8.wireOp",EDGE,"E40"),sQuery(id+"F17.wireOp",EDGE,"E64.left")])],"isStart":false}),makeQuery(id+"F36.opExtrude","CAP_FACE",FACE,{"disambiguationData":[OSD([sQuery(id+"F35.wireOp",EDGE,"E95.0"),sQuery(id+"F35.wireOp",EDGE,"E96"),sQuery(id+"F35.wireOp",EDGE,"E97")])],"isStart":true}),makeQuery(id+"F36.opExtrude","CAP_FACE",FACE,{"disambiguationData":[OSD([sQuery(id+"F35.wireOp",EDGE,"E99.MirrorCS"),sQuery(id+"F35.wireOp",EDGE,"E100.MirrorCS"),sQuery(id+"F35.wireOp",EDGE,"E101.MirrorCS")])],"isStart":true})]});
            var sketch = newSketch(context, id + "F37", { "sketchPlane" : qUnion([Q0])});
            skLineSegment(sketch, "E102.bottom", {"start": v(-13.5, 12.5) * mm, "end": v(13.5, 12.5) * mm});
            skLineSegment(sketch, "E102.top", {"start": v(-13.5, 7.75) * mm, "end": v(13.5, 7.75) * mm});
            skLineSegment(sketch, "E102.left", {"start": v(-13.5, 12.5) * mm, "end": v(-13.5, 7.75) * mm});
            skLineSegment(sketch, "E102.right", {"start": v(13.5, 12.5) * mm, "end": v(13.5, 7.75) * mm});
            skSolve(sketch);
        }
        {
            var Q0;
            Q0 = qSketchRegion(id + "F37", true);
            extrude(context, id + "F38", {"entities" : qUnion([Q0]), "operationType" : NewBodyOperationType.REMOVE, "endBound" : BoundingType.THROUGH_ALL, "oppositeDirection" : true, "depth" : 25 * mm});
        }
        {
            var Q0;
            Q0=makeQuery(id+"F30.opExtrude","CAP_EDGE",EDGE,{"disambiguationData":[OSD([sQuery(id+"F8.wireOp",EDGE,"E32.0"),sQuery(id+"F8.wireOp",EDGE,"E32.1"),sQuery(id+"F8.wireOp",EDGE,"E32.2"),sQuery(id+"F8.wireOp",EDGE,"E32.3"),sQuery(id+"F8.wireOp",EDGE,"E32.4"),sQuery(id+"F8.wireOp",EDGE,"E33"),sQuery(id+"F8.wireOp",EDGE,"E34"),sQuery(id+"F8.wireOp",EDGE,"E36"),sQuery(id+"F8.wireOp",EDGE,"E37.MirrorCS"),sQuery(id+"F8.wireOp",EDGE,"E38.MirrorCS"),sQuery(id+"F8.wireOp",EDGE,"E39.MirrorCS"),sQuery(id+"F8.wireOp",EDGE,"E40"),sQuery(id+"F17.wireOp",EDGE,"E64.left"),sQuery(id+"F19.wireOp",EDGE,"E66.top")])],"isStart":false});
            var Q1;
            {var subQ0=sQuery(id+"F8.wireOp",EDGE,"E34");var subQ15=sQuery(id+"F37.wireOp",EDGE,"E102.top");Q1=makeQuery(id+"F38.boolean.opBoolean","COPY",EDGE,{"disambiguationData":[TD([makeQuery(id+"F9.opExtrude","SWEPT_FACE",FACE,{"disambiguationData":[OSD([subQ0])]})])],"derivedFrom":makeQuery(id+"F38.opExtrude","CAP_EDGE",EDGE,{"disambiguationData":[OSD([subQ15])],"isStart":true})});}
            var Q2;
            {var subQ0=sQuery(id+"F8.wireOp",EDGE,"E38.MirrorCS");var subQ15=sQuery(id+"F37.wireOp",EDGE,"E102.top");Q2=makeQuery(id+"F38.boolean.opBoolean","COPY",EDGE,{"disambiguationData":[TD([makeQuery(id+"F9.opExtrude","SWEPT_FACE",FACE,{"disambiguationData":[OSD([subQ0])]})])],"derivedFrom":makeQuery(id+"F38.opExtrude","CAP_EDGE",EDGE,{"disambiguationData":[OSD([subQ15])],"isStart":true})});}
            chamfer(context, id + "F39", {"entities" : qUnion([Q0, Q1, Q2]), "width" : 5 * mm, "tangentPropagation" : true});
        }
        {
            var Q0;
            {var subQ0=sQuery(id+"F19.wireOp",EDGE,"E66.top");Q0=makeQuery(id+"F34.boolean.opBoolean","INTERSECT",EDGE,{"disambiguationData":[OD(0.0)],"derivedFrom":[makeQuery(id+"F30.boolean.opBoolean","MERGE",FACE,{"derivedFrom":[makeQuery(id+"F20.boolean.opBoolean","COPY",FACE,{"derivedFrom":makeQuery(id+"F20.opExtrude","SWEPT_FACE",FACE,{"disambiguationData":[OSD([subQ0])]})}),makeQuery(id+"F30.opExtrude","SWEPT_FACE",FACE,{"disambiguationData":[OSD([sQuery(id+"F8.wireOp",EDGE,"E32.0"),sQuery(id+"F8.wireOp",EDGE,"E32.1"),sQuery(id+"F8.wireOp",EDGE,"E32.2"),sQuery(id+"F8.wireOp",EDGE,"E32.3"),sQuery(id+"F8.wireOp",EDGE,"E32.4"),sQuery(id+"F8.wireOp",EDGE,"E33"),sQuery(id+"F8.wireOp",EDGE,"E34"),sQuery(id+"F8.wireOp",EDGE,"E36"),sQuery(id+"F8.wireOp",EDGE,"E37.MirrorCS"),sQuery(id+"F8.wireOp",EDGE,"E38.MirrorCS"),sQuery(id+"F8.wireOp",EDGE,"E39.MirrorCS"),sQuery(id+"F8.wireOp",EDGE,"E40"),sQuery(id+"F17.wireOp",EDGE,"E64.left"),subQ0])]})]}),makeQuery(id+"F34.opExtrude","SWEPT_FACE",FACE,{"disambiguationData":[OSD([sQuery(id+"F33.wireOp",EDGE,"E93")])]})]});}
            var Q1;
            {var subQ0=sQuery(id+"F19.wireOp",EDGE,"E66.top");Q1=makeQuery(id+"F34.boolean.opBoolean","INTERSECT",EDGE,{"disambiguationData":[OD(1.0)],"derivedFrom":[makeQuery(id+"F30.boolean.opBoolean","MERGE",FACE,{"derivedFrom":[makeQuery(id+"F20.boolean.opBoolean","COPY",FACE,{"derivedFrom":makeQuery(id+"F20.opExtrude","SWEPT_FACE",FACE,{"disambiguationData":[OSD([subQ0])]})}),makeQuery(id+"F30.opExtrude","SWEPT_FACE",FACE,{"disambiguationData":[OSD([sQuery(id+"F8.wireOp",EDGE,"E32.0"),sQuery(id+"F8.wireOp",EDGE,"E32.1"),sQuery(id+"F8.wireOp",EDGE,"E32.2"),sQuery(id+"F8.wireOp",EDGE,"E32.3"),sQuery(id+"F8.wireOp",EDGE,"E32.4"),sQuery(id+"F8.wireOp",EDGE,"E33"),sQuery(id+"F8.wireOp",EDGE,"E34"),sQuery(id+"F8.wireOp",EDGE,"E36"),sQuery(id+"F8.wireOp",EDGE,"E37.MirrorCS"),sQuery(id+"F8.wireOp",EDGE,"E38.MirrorCS"),sQuery(id+"F8.wireOp",EDGE,"E39.MirrorCS"),sQuery(id+"F8.wireOp",EDGE,"E40"),sQuery(id+"F17.wireOp",EDGE,"E64.left"),subQ0])]})]}),makeQuery(id+"F34.opExtrude","SWEPT_FACE",FACE,{"disambiguationData":[OSD([sQuery(id+"F33.wireOp",EDGE,"E93")])]})]});}
            fillet(context, id + "F40", {"entities" : qUnion([Q0, Q1]), "radius" : 5 * mm, "tangentPropagation" : true, "allowEdgeOverflow" : false});
        }
        {
            var Q0;
            Q0=makeQuery(id+"F23.boolean.opBoolean","COPY",EDGE,{"derivedFrom":makeQuery(id+"F23.opExtrude","CAP_EDGE",EDGE,{"disambiguationData":[OSD([sQuery(id+"F22.wireOp",EDGE,"E69")])],"isStart":true})});
            var Q1;
            Q1=makeQuery(id+"F23.boolean.opBoolean","COPY",EDGE,{"derivedFrom":makeQuery(id+"F23.opExtrude","CAP_EDGE",EDGE,{"disambiguationData":[OSD([sQuery(id+"F22.wireOp",EDGE,"E70")])],"isStart":true})});
            var Q2;
            Q2=makeQuery(id+"F5.boolean.opBoolean","COPY",EDGE,{"derivedFrom":makeQuery(id+"F5.opExtrude","CAP_EDGE",EDGE,{"disambiguationData":[OSD([sQuery(id+"F4.wireOp",EDGE,"E26")])],"isStart":true})});
            var Q3;
            Q3=makeQuery(id+"F5.boolean.opBoolean","COPY",EDGE,{"derivedFrom":makeQuery(id+"F5.opExtrude","CAP_EDGE",EDGE,{"disambiguationData":[OSD([sQuery(id+"F4.wireOp",EDGE,"E27")])],"isStart":true})});
            var Q4;
            Q4=makeQuery(id+"F23.boolean.opBoolean","INTERSECT",EDGE,{"derivedFrom":[makeQuery(id+"F9.opExtrude","SWEPT_FACE",FACE,{"disambiguationData":[OSD([sQuery(id+"F8.wireOp",EDGE,"E38.MirrorCS")])]}),makeQuery(id+"F23.opExtrude","SWEPT_FACE",FACE,{"disambiguationData":[OSD([sQuery(id+"F22.wireOp",EDGE,"E70")])]})]});
            var Q5;
            Q5=makeQuery(id+"F23.boolean.opBoolean","INTERSECT",EDGE,{"derivedFrom":[makeQuery(id+"F9.opExtrude","SWEPT_FACE",FACE,{"disambiguationData":[OSD([sQuery(id+"F8.wireOp",EDGE,"E38.MirrorCS")])]}),makeQuery(id+"F23.opExtrude","SWEPT_FACE",FACE,{"disambiguationData":[OSD([sQuery(id+"F22.wireOp",EDGE,"E69")])]})]});
            var Q6;
            Q6=makeQuery(id+"F7.boolean.opBoolean","COPY",EDGE,{"derivedFrom":makeQuery(id+"F7.opExtrude","CAP_EDGE",EDGE,{"disambiguationData":[OSD([sQuery(id+"F6.wireOp",EDGE,"E31")])],"isStart":true})});
            var Q7;
            Q7=makeQuery(id+"F7.boolean.opBoolean","COPY",EDGE,{"derivedFrom":makeQuery(id+"F7.opExtrude","CAP_EDGE",EDGE,{"disambiguationData":[OSD([sQuery(id+"F6.wireOp",EDGE,"E30")])],"isStart":true})});
            chamfer(context, id + "F41", {"entities" : qUnion([Q0, Q1, Q2, Q3, Q4, Q5, Q6, Q7]), "width" : 2 * mm, "tangentPropagation" : true});
        }
    });
